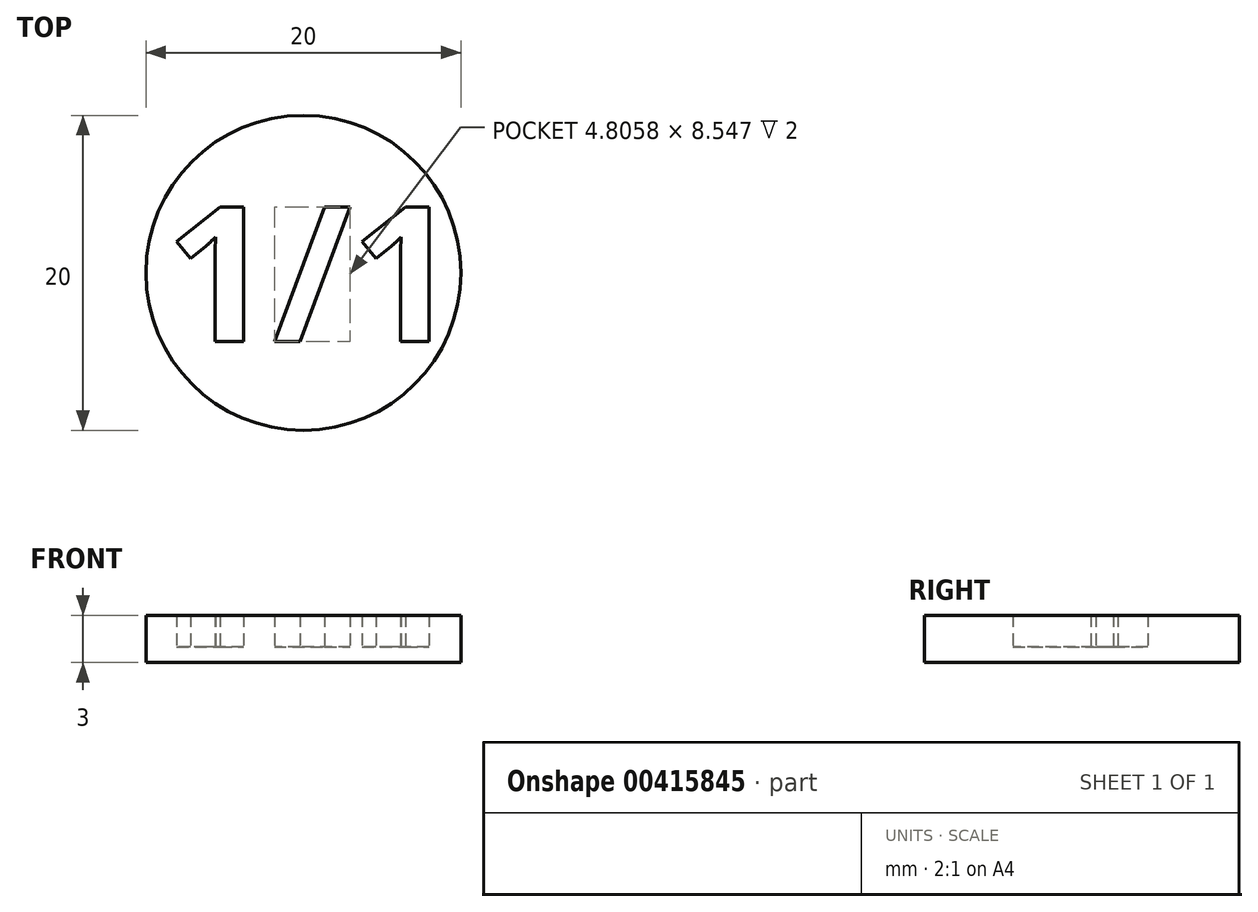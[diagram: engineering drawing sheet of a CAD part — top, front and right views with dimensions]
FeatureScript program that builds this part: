
annotation { "Feature Type Name" : "Feature", "Feature Type Description" : "" }
export const myFeature = defineFeature(function(context is Context, id is Id, definition is map)
    precondition{}
    {
        {
            var Q0;
            Q0=qCreatedBy(makeId("Top.planeOp"),FACE);
            var sketch = newSketch(context, id + "F0", { "sketchPlane" : qUnion([Q0])});
            skCircle(sketch, "E0", {"center": v(0, 0) * mm, "radius": 10 * mm});
            skLineSegment(sketch, "E1.bottom", {"start": v(-8.75, 4.26) * mm, "end": v(8.75, 4.26) * mm});
            skLineSegment(sketch, "E1.top", {"start": v(-8.75, -4.36) * mm, "end": v(8.75, -4.36) * mm});
            skLineSegment(sketch, "E1.left", {"start": v(-8.75, 4.26) * mm, "end": v(-8.75, -4.36) * mm});
            skLineSegment(sketch, "E1.right", {"start": v(8.75, 4.26) * mm, "end": v(8.75, -4.36) * mm});
            skText(sketch, "E2", { "text": "1/1", "fontName": "OpenSans-Bold.ttf"});
            const initialGuessF0  = {"E2": [-0.00875, -0.00436, 1, 0, 0.00862]};
            skSetInitialGuess(sketch, initialGuessF0);
            skSolve(sketch);
        }
        {
            var Q0;
            Q0=makeQuery(id+"F0.imprint","IMPRINT",FACE,{"disambiguationData":[TD([[makeQuery(id+"F0.imprint","IMPRINT",EDGE,{"derivedFrom":sQuery(id+"F0.wireOp",EDGE,"E0")}),1.0]])]});
            var Q1;
            Q1=makeQuery(id+"F0.imprint","IMPRINT",FACE,{"disambiguationData":[TD([[makeQuery(id+"F0.imprint","IMPRINT",EDGE,{"derivedFrom":sQuery(id+"F0.wireOp",EDGE,"E1.bottom")}),-1.0]])]});
            extrude(context, id + "F1", {"entities" : qUnion([Q0, Q1]), "depth" : 3 * mm});
        }
        {
            var Q0;
            Q0=qCreatedBy(makeId("Top.planeOp"),FACE);
            var sketch = newSketch(context, id + "F2", { "sketchPlane" : qUnion([Q0])});
            skCircle(sketch, "E3", {"center": v(0, 0) * mm, "radius": 10 * mm});
            skSolve(sketch);
        }
        {
            var Q0;
            Q0 = qSketchRegion(id + "F2", true);
            extrude(context, id + "F3", {"entities" : qUnion([Q0]), "operationType" : NewBodyOperationType.ADD, "depth" : 1 * mm});
        }
    });
